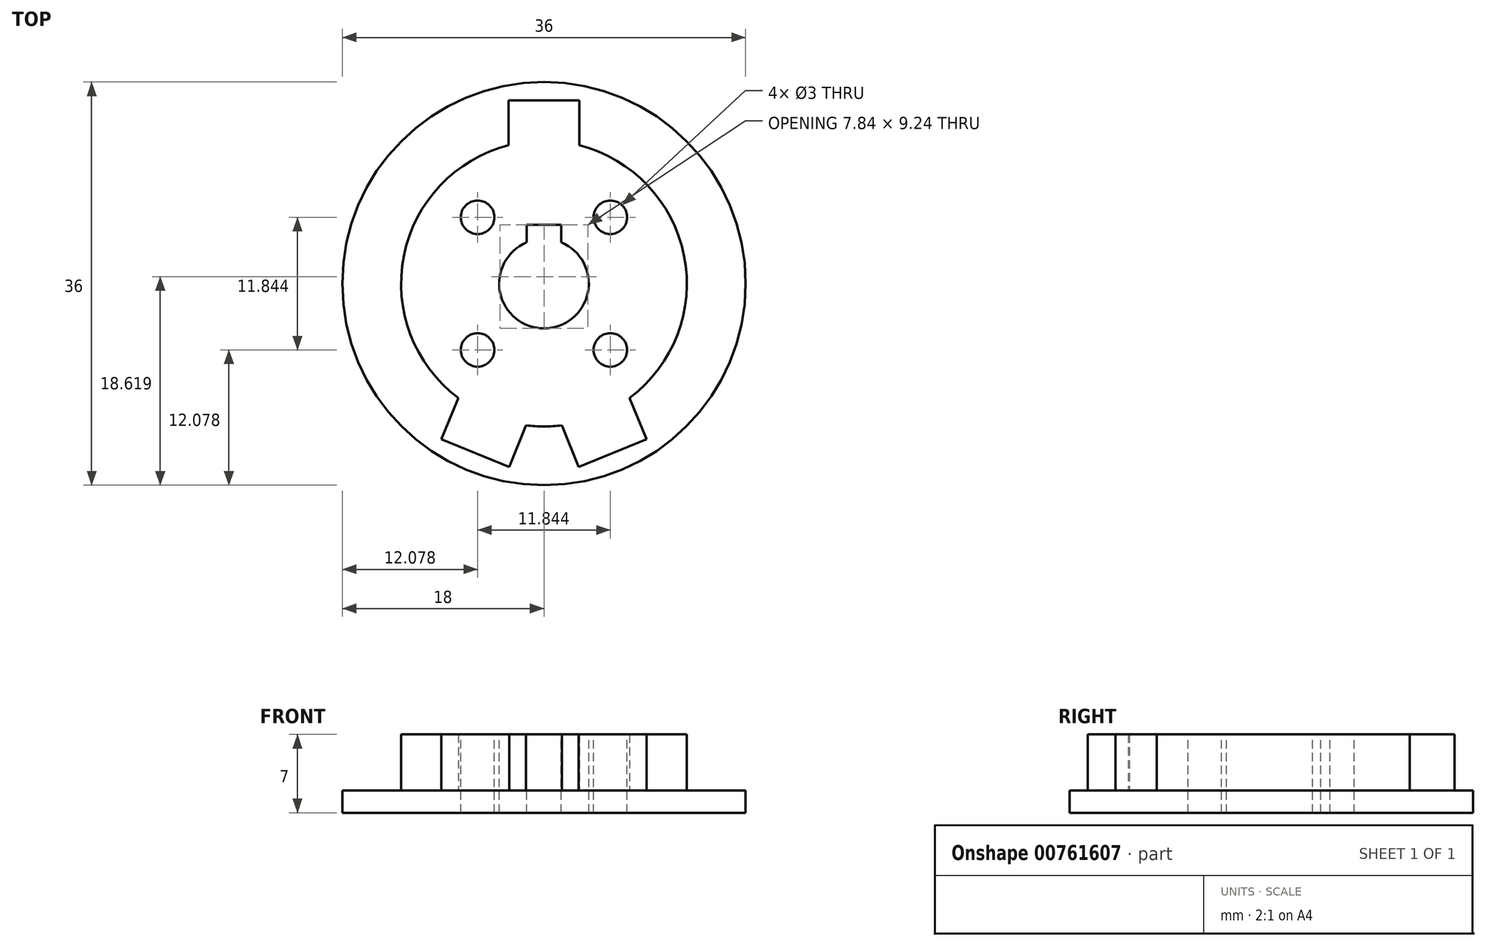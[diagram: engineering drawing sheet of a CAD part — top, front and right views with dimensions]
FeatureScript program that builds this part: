
annotation { "Feature Type Name" : "Feature", "Feature Type Description" : "" }
export const myFeature = defineFeature(function(context is Context, id is Id, definition is map)
    precondition{}
    {
        {
            var Q0;
            Q0=qCreatedBy(makeId("Top.planeOp"),FACE);
            var sketch = newSketch(context, id + "F0", { "sketchPlane" : qUnion([Q0])});
            skArc(sketch, "E0", {"start": v(7.65, -10.2) * mm, "mid": v(12.5, 2.5) * mm, "end": v(3.15, 12.35) * mm});
            skLineSegment(sketch, "E1", {"start": v(0, 12.75) * mm, "end": v(0, -12.75) * mm, "construction": true});
            skLineSegment(sketch, "E2", {"start": v(-3.15, 16.35) * mm, "end": v(0, 16.35) * mm});
            skLineSegment(sketch, "E3", {"start": v(0, 16.35) * mm, "end": v(3.15, 16.35) * mm});
            skLineSegment(sketch, "E4", {"start": v(-3.15, 16.35) * mm, "end": v(-3.15, 12.35) * mm});
            skLineSegment(sketch, "E5", {"start": v(3.15, 16.35) * mm, "end": v(3.15, 12.35) * mm});
            skLineSegment(sketch, "E6", {"start": v(1.6, -12.65) * mm, "end": v(7.65, -10.2) * mm, "construction": true});
            skLineSegment(sketch, "E7", {"start": v(1.6, -12.65) * mm, "end": v(3.1, -16.36) * mm});
            skLineSegment(sketch, "E8", {"start": v(7.65, -10.2) * mm, "end": v(9.15, -13.9) * mm});
            skLineSegment(sketch, "E9", {"start": v(3.1, -16.36) * mm, "end": v(9.15, -13.9) * mm});
            skLineSegment(sketch, "E10.MirrorCS", {"start": v(-1.6, -12.65) * mm, "end": v(-3.1, -16.36) * mm});
            skLineSegment(sketch, "E11.MirrorCS", {"start": v(-3.1, -16.36) * mm, "end": v(-9.15, -13.9) * mm});
            skLineSegment(sketch, "E12.MirrorCS", {"start": v(-7.65, -10.2) * mm, "end": v(-9.15, -13.9) * mm});
            skArc(sketch, "E13.trimOffspring", {"start": v(-1.6, -12.65) * mm, "mid": v(0, -12.75) * mm, "end": v(1.6, -12.65) * mm});
            skArc(sketch, "E14.trimOffspring", {"start": v(-3.15, 12.35) * mm, "mid": v(-12.5, 2.5) * mm, "end": v(-7.65, -10.2) * mm});
            skLineSegment(sketch, "E15", {"start": v(-1.6, -12.65) * mm, "end": v(1.6, -12.65) * mm, "construction": true});
            skLineSegment(sketch, "E16", {"start": v(-3.1, -16.36) * mm, "end": v(3.1, -16.36) * mm, "construction": true});
            skLineSegment(sketch, "E17", {"start": v(-9.15, -13.9) * mm, "end": v(9.15, -13.9) * mm, "construction": true});
            skLineSegment(sketch, "E18", {"start": v(-7.65, -10.2) * mm, "end": v(7.65, -10.2) * mm, "construction": true});
            skSolve(sketch);
        }
        {
            var Q0;
            Q0=qSketchRegion(id+"F0",true);
            extrude(context, id + "F1", {"entities" : qUnion([Q0]), "depth" : 5 * mm, "offsetDistance" : 25 * mm});
        }
        {
            var Q0;
            Q0=makeQuery(id+"F1.opExtrude","CAP_FACE",FACE,{"disambiguationData":[OSD([sQuery(id+"F0.wireOp",EDGE,"E0"),sQuery(id+"F0.wireOp",EDGE,"E2"),sQuery(id+"F0.wireOp",EDGE,"E3"),sQuery(id+"F0.wireOp",EDGE,"E4"),sQuery(id+"F0.wireOp",EDGE,"E5"),sQuery(id+"F0.wireOp",EDGE,"E7"),sQuery(id+"F0.wireOp",EDGE,"E8"),sQuery(id+"F0.wireOp",EDGE,"E9"),sQuery(id+"F0.wireOp",EDGE,"E10.MirrorCS"),sQuery(id+"F0.wireOp",EDGE,"E11.MirrorCS"),sQuery(id+"F0.wireOp",EDGE,"E12.MirrorCS"),sQuery(id+"F0.wireOp",EDGE,"E13.trimOffspring"),sQuery(id+"F0.wireOp",EDGE,"E14.trimOffspring")])],"isStart":true});
            var sketch = newSketch(context, id + "F2", { "sketchPlane" : qUnion([Q0])});
            skCircle(sketch, "E19", {"center": v(0, 0) * mm, "radius": 18 * mm});
            skSolve(sketch);
        }
        {
            var Q0;
            Q0 = qSketchRegion(id + "F2", true);
            extrude(context, id + "F3", {"entities" : qUnion([Q0]), "operationType" : NewBodyOperationType.ADD, "depth" : 2 * mm, "offsetDistance" : 25 * mm});
        }
        {
            var Q0;
            Q0=makeQuery(id+"F1.opExtrude","CAP_FACE",FACE,{"disambiguationData":[OSD([sQuery(id+"F0.wireOp",EDGE,"E0"),sQuery(id+"F0.wireOp",EDGE,"E2"),sQuery(id+"F0.wireOp",EDGE,"E3"),sQuery(id+"F0.wireOp",EDGE,"E4"),sQuery(id+"F0.wireOp",EDGE,"E5"),sQuery(id+"F0.wireOp",EDGE,"E7"),sQuery(id+"F0.wireOp",EDGE,"E8"),sQuery(id+"F0.wireOp",EDGE,"E9"),sQuery(id+"F0.wireOp",EDGE,"E10.MirrorCS"),sQuery(id+"F0.wireOp",EDGE,"E11.MirrorCS"),sQuery(id+"F0.wireOp",EDGE,"E12.MirrorCS"),sQuery(id+"F0.wireOp",EDGE,"E13.trimOffspring"),sQuery(id+"F0.wireOp",EDGE,"E14.trimOffspring")])],"isStart":false});
            var sketch = newSketch(context, id + "F4", { "sketchPlane" : qUnion([Q0])});
            skArc(sketch, "E20", {"start": v(-1.55, 3.69) * mm, "mid": v(0, -4) * mm, "end": v(1.55, 3.69) * mm});
            skLineSegment(sketch, "E21", {"start": v(0, 4) * mm, "end": v(0, 5.24) * mm, "construction": true});
            skLineSegment(sketch, "E22", {"start": v(0, 5.24) * mm, "end": v(1.55, 5.24) * mm});
            skLineSegment(sketch, "E23", {"start": v(0, 5.24) * mm, "end": v(-1.55, 5.24) * mm});
            skLineSegment(sketch, "E24", {"start": v(1.55, 5.24) * mm, "end": v(1.55, 3.69) * mm});
            skLineSegment(sketch, "E25", {"start": v(-1.55, 5.24) * mm, "end": v(-1.55, 3.69) * mm});
            skLineSegment(sketch, "E26", {"start": v(-12.75, 0) * mm, "end": v(0, 0) * mm, "construction": true});
            skLineSegment(sketch, "E27", {"start": v(0, 0) * mm, "end": v(-2.83, 2.83) * mm, "construction": true});
            skLineSegment(sketch, "E28", {"start": v(0, 0) * mm, "end": v(8.84, -8.84) * mm, "construction": true});
            skLineSegment(sketch, "E29.MirrorCS", {"start": v(0, 0) * mm, "end": v(8.84, 8.84) * mm, "construction": true});
            skLineSegment(sketch, "E30.MirrorCS", {"start": v(0, 0) * mm, "end": v(-9.02, -9.02) * mm, "construction": true});
            skCircle(sketch, "E31", {"center": v(-5.92, 5.92) * mm, "radius": 1.5 * mm});
            skCircle(sketch, "E32.1.0", {"center": v(-5.92, -5.92) * mm, "radius": 1.5 * mm});
            skCircle(sketch, "E32.2.0", {"center": v(5.92, -5.92) * mm, "radius": 1.5 * mm});
            skCircle(sketch, "E32.3.0", {"center": v(5.92, 5.92) * mm, "radius": 1.5 * mm});
            skLineSegment(sketch, "E33", {"start": v(-2.83, 2.83) * mm, "end": v(-9.02, 9.02) * mm, "construction": true});
            skSolve(sketch);
        }
        {
            var Q0;
            Q0=qSketchRegion(id+"F4",true);
            var Q1;
            Q1=makeQuery(id+"F3.opExtrude","CAP_FACE",FACE,{"disambiguationData":[OSD([sQuery(id+"F2.wireOp",EDGE,"E19")])],"isStart":false});
            extrude(context, id + "F5", {"entities" : qUnion([Q0]), "operationType" : NewBodyOperationType.REMOVE, "endBound" : BoundingType.UP_TO_SURFACE, "oppositeDirection" : true, "depth" : 25 * mm, "endBoundEntityFace" : qUnion([Q1]), "offsetDistance" : 25 * mm});
        }
    });
